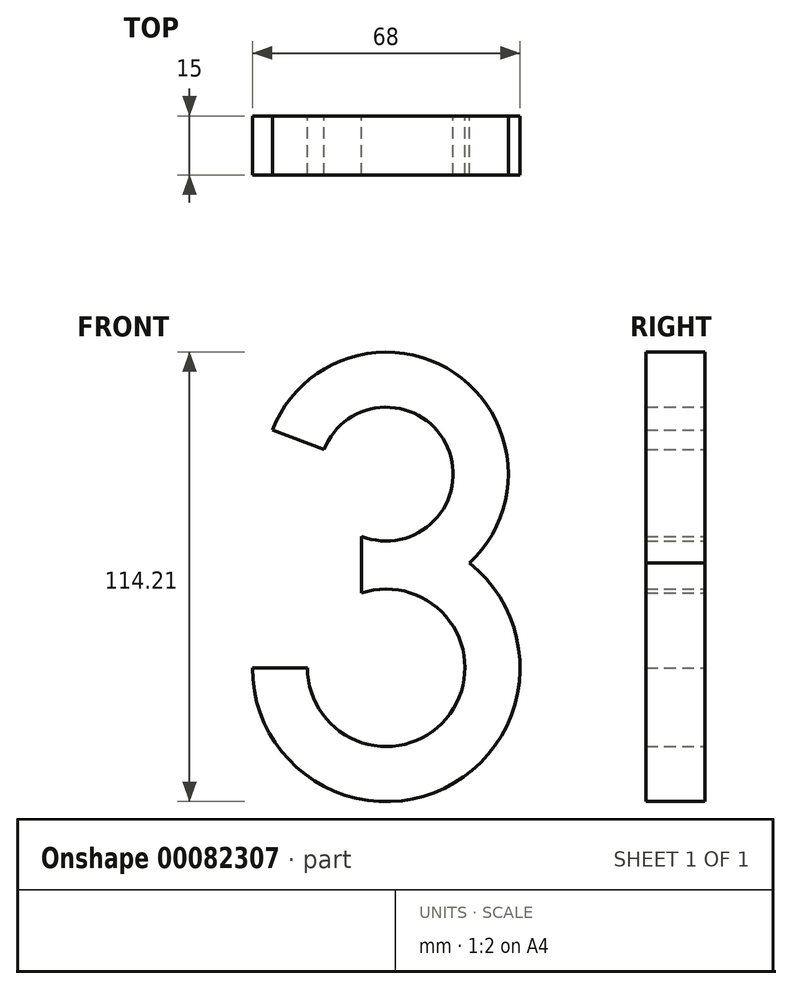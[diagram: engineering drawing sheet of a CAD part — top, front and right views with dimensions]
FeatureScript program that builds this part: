
annotation { "Feature Type Name" : "Feature", "Feature Type Description" : "" }
export const myFeature = defineFeature(function(context is Context, id is Id, definition is map)
    precondition{}
    {
        {
            var Q0;
            Q0=qCreatedBy(makeId("Front.planeOp"),FACE);
            var sketch = newSketch(context, id + "F0", { "sketchPlane" : qUnion([Q0])});
            skArc(sketch, "E0", {"start": v(21.2, -22.62) * mm, "mid": v(17.32, 25.7) * mm, "end": v(-28.93, 11.15) * mm});
            skArc(sketch, "E1", {"start": v(-6.28, -15.8) * mm, "mid": v(15.6, 6.75) * mm, "end": v(-15.81, 6.24) * mm});
            skArc(sketch, "E2", {"start": v(-34, -49.2) * mm, "mid": v(14.75, -79.84) * mm, "end": v(21.2, -22.62) * mm});
            skArc(sketch, "E3", {"start": v(-20, -49.2) * mm, "mid": v(16.2, -60.93) * mm, "end": v(-6.28, -30.22) * mm});
            skLineSegment(sketch, "E4", {"start": v(-15.81, 6.24) * mm, "end": v(-28.93, 11.15) * mm});
            skLineSegment(sketch, "E5", {"start": v(-20, -49.2) * mm, "end": v(-34, -49.2) * mm});
            skLineSegment(sketch, "E6", {"start": v(-6.28, -15.8) * mm, "end": v(-6.28, -30.22) * mm});
            skSolve(sketch);
        }
        {
            var Q0;
            Q0=makeQuery(id+"F0.imprint","IMPRINT",FACE,{"disambiguationData":[TD([[makeQuery(id+"F0.imprint","IMPRINT",EDGE,{"derivedFrom":sQuery(id+"F0.wireOp",EDGE,"E0")}),1.0]])]});
            extrude(context, id + "F1", {"entities" : qUnion([Q0]), "depth" : 15 * mm});
        }
    });
